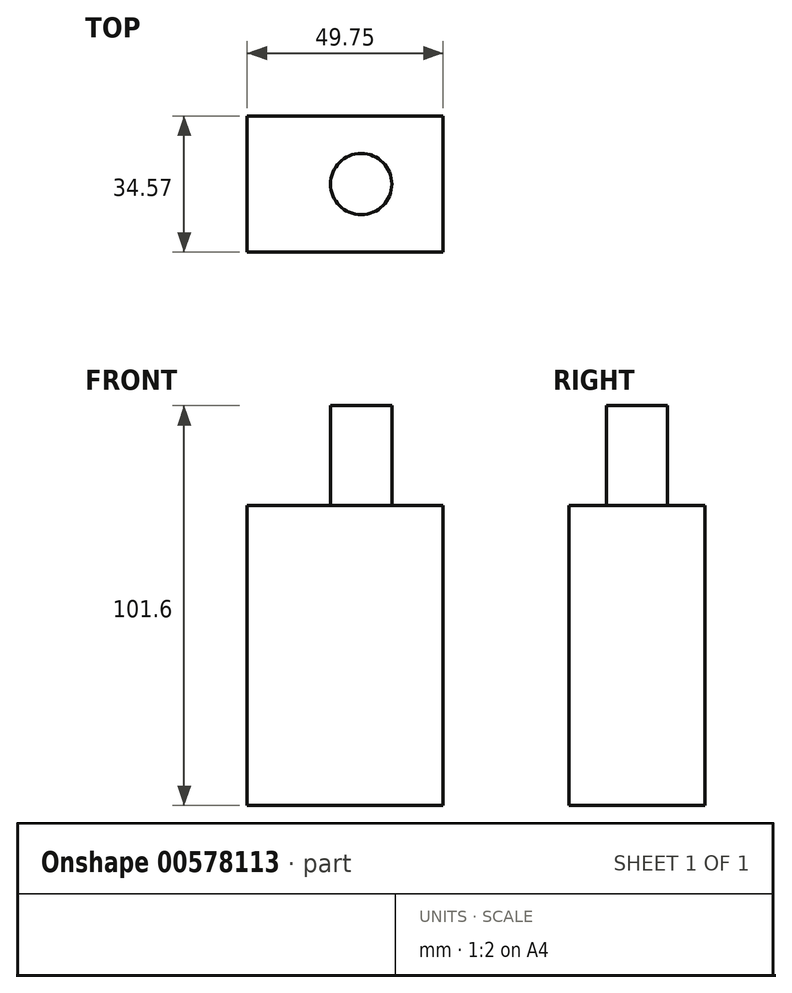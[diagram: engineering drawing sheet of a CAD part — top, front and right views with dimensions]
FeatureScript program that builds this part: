
annotation { "Feature Type Name" : "Feature", "Feature Type Description" : "" }
export const myFeature = defineFeature(function(context is Context, id is Id, definition is map)
    precondition{}
    {
        {
            var Q0;
            Q0=qCreatedBy(makeId("Top.planeOp"),FACE);
            var sketch = newSketch(context, id + "F0", { "sketchPlane" : qUnion([Q0])});
            skLineSegment(sketch, "E0.bottom", {"start": v(0, 0) * mm, "end": v(49.75, 0) * mm});
            skLineSegment(sketch, "E0.top", {"start": v(0, -34.57) * mm, "end": v(49.75, -34.57) * mm});
            skLineSegment(sketch, "E0.left", {"start": v(0, 0) * mm, "end": v(0, -34.57) * mm});
            skLineSegment(sketch, "E0.right", {"start": v(49.75, 0) * mm, "end": v(49.75, -34.57) * mm});
            skSolve(sketch);
        }
        {
            var Q0;
            Q0=makeQuery(id+"F0.imprint","IMPRINT",FACE,{"disambiguationData":[TD([[makeQuery(id+"F0.imprint","IMPRINT",EDGE,{"derivedFrom":sQuery(id+"F0.wireOp",EDGE,"E0.bottom")}),-1.0]])]});
            extrude(context, id + "F1", {"entities" : qUnion([Q0]), "depth" : 76.2 * mm, "offsetDistance" : 25.4 * mm});
        }
        {
            var Q0;
            Q0=makeQuery(id+"F1.opExtrude","CAP_FACE",FACE,{"disambiguationData":[OSD([sQuery(id+"F0.wireOp",EDGE,"E0.bottom"),sQuery(id+"F0.wireOp",EDGE,"E0.top"),sQuery(id+"F0.wireOp",EDGE,"E0.left"),sQuery(id+"F0.wireOp",EDGE,"E0.right")])],"isStart":false});
            var sketch = newSketch(context, id + "F2", { "sketchPlane" : qUnion([Q0])});
            skCircle(sketch, "E1", {"center": v(28.96, -17.28) * mm, "radius": 7.78 * mm});
            skPoint(sketch, "E1.centerSnap0", {"position": v(0, -17.28) * mm});
            skSolve(sketch);
        }
        {
            var Q0;
            Q0 = qSketchRegion(id + "F2", true);
            extrude(context, id + "F3", {"entities" : qUnion([Q0]), "operationType" : NewBodyOperationType.ADD, "depth" : 25.4 * mm, "offsetDistance" : 25.4 * mm});
        }
    });
